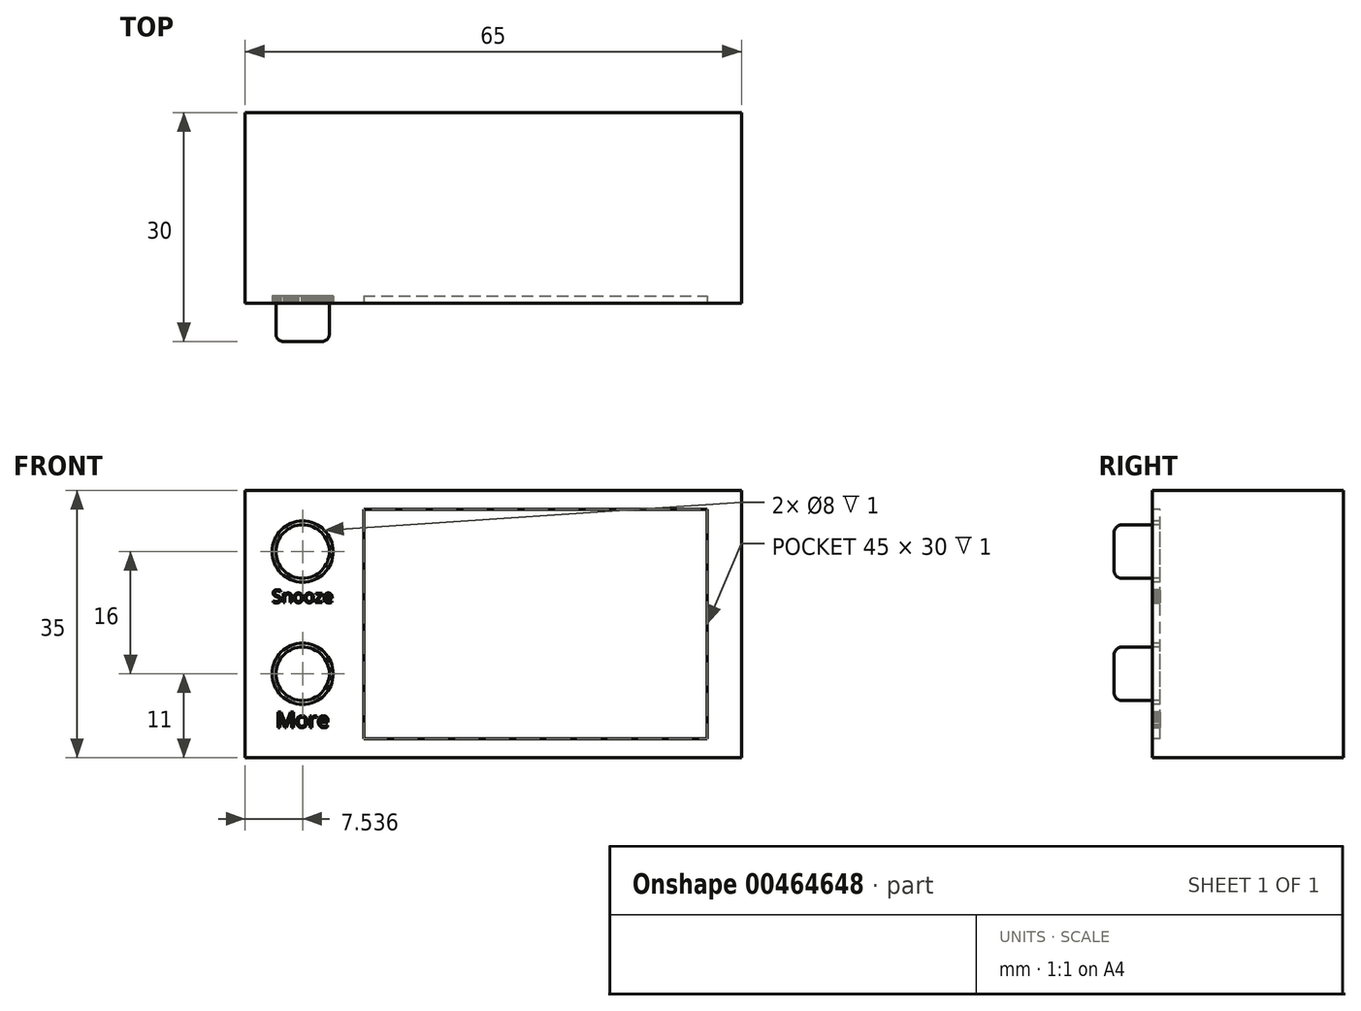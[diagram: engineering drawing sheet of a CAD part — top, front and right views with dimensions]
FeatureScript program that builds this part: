
annotation { "Feature Type Name" : "Feature", "Feature Type Description" : "" }
export const myFeature = defineFeature(function(context is Context, id is Id, definition is map)
    precondition{}
    {
        {
            var Q0;
            Q0=qCreatedBy(makeId("Front.planeOp"),FACE);
            var sketch = newSketch(context, id + "F0", { "sketchPlane" : qUnion([Q0])});
            skLineSegment(sketch, "E0.bottom", {"start": v(-32.5, 17.5) * mm, "end": v(32.5, 17.5) * mm});
            skLineSegment(sketch, "E0.top", {"start": v(-32.5, -17.5) * mm, "end": v(32.5, -17.5) * mm});
            skLineSegment(sketch, "E0.left", {"start": v(-32.5, 17.5) * mm, "end": v(-32.5, -17.5) * mm});
            skLineSegment(sketch, "E0.right", {"start": v(32.5, 17.5) * mm, "end": v(32.5, -17.5) * mm});
            skPoint(sketch, "E0.middle", {"position": v(0, 0) * mm});
            skPoint(sketch, "E1", {"position": v(0, 17.5) * mm});
            skPoint(sketch, "E2.middle", {"position": v(5.71, 0) * mm});
            skSolve(sketch);
        }
        {
            var Q0;
            Q0=makeQuery(id+"F0.imprint","IMPRINT",FACE,{"disambiguationData":[TD([[makeQuery(id+"F0.imprint","IMPRINT",EDGE,{"derivedFrom":sQuery(id+"F0.wireOp",EDGE,"E0.bottom")}),-1.0]])]});
            extrude(context, id + "F1", {"entities" : qUnion([Q0]), "oppositeDirection" : true, "depth" : 25 * mm});
        }
        {
            var Q0;
            Q0=qCreatedBy(makeId("Front.planeOp"),FACE);
            var sketch = newSketch(context, id + "F2", { "sketchPlane" : qUnion([Q0])});
            skLineSegment(sketch, "E3.bottom", {"start": v(-32.5, 17.5) * mm, "end": v(32.5, 17.5) * mm});
            skLineSegment(sketch, "E3.top", {"start": v(-32.5, -17.5) * mm, "end": v(32.5, -17.5) * mm});
            skLineSegment(sketch, "E3.left", {"start": v(-32.5, 17.5) * mm, "end": v(-32.5, -17.5) * mm});
            skLineSegment(sketch, "E3.right", {"start": v(32.5, 17.5) * mm, "end": v(32.5, -17.5) * mm});
            skPoint(sketch, "E3.middle", {"position": v(0, 0) * mm});
            skPoint(sketch, "E4", {"position": v(0, 17.5) * mm});
            skLineSegment(sketch, "E5.bottom", {"start": v(-16.96, -15) * mm, "end": v(28.04, -15) * mm});
            skLineSegment(sketch, "E5.top", {"start": v(-16.96, 15) * mm, "end": v(28.04, 15) * mm});
            skLineSegment(sketch, "E5.left", {"start": v(-16.96, -15) * mm, "end": v(-16.96, 15) * mm});
            skLineSegment(sketch, "E5.right", {"start": v(28.04, -15) * mm, "end": v(28.04, 15) * mm});
            skPoint(sketch, "E5.middle", {"position": v(5.54, 0) * mm});
            skCircle(sketch, "E6", {"center": v(-24.96, 9.5) * mm, "radius": 4 * mm});
            skCircle(sketch, "E7", {"center": v(-24.96, -6.5) * mm, "radius": 4 * mm});
            skText(sketch, "E8", { "text": "Snooze\n", "fontName": "OpenSans-Regular.ttf"});
            skText(sketch, "E9", { "text": "More\n", "fontName": "OpenSans-Regular.ttf"});
            skCircle(sketch, "E10", {"center": v(-24.96, 9.5) * mm, "radius": 3.5 * mm});
            skCircle(sketch, "E11", {"center": v(-24.96, -6.5) * mm, "radius": 3.5 * mm});
            const initialGuessF2  = {"E8": [-0.02896, 0.00281, 1, 0, 0.00169], "E9": [-0.02846, -0.01353, 1, 0, 0.00203]};
            skSetInitialGuess(sketch, initialGuessF2);
            skSolve(sketch);
        }
        {
            var Q0;
            Q0=makeQuery(id+"F2.imprint","IMPRINT",FACE,{"disambiguationData":[TD([[makeQuery(id+"F2.imprint","IMPRINT",EDGE,{"derivedFrom":sQuery(id+"F2.wireOp",EDGE,"E5.bottom")}),1.0]])]});
            extrude(context, id + "F3", {"entities" : qUnion([Q0]), "operationType" : NewBodyOperationType.REMOVE, "oppositeDirection" : true, "depth" : 1 * mm});
        }
        {
            var Q0;
            Q0=makeQuery(id+"F2.imprint","IMPRINT",FACE,{"disambiguationData":[TD([[makeQuery(id+"F2.imprint","IMPRINT",EDGE,{"derivedFrom":sQuery(id+"F2.wireOp",EDGE,"E6")}),1.0]])]});
            var Q1;
            Q1=makeQuery(id+"F2.imprint","IMPRINT",FACE,{"disambiguationData":[TD([[makeQuery(id+"F2.imprint","IMPRINT",EDGE,{"derivedFrom":sQuery(id+"F2.wireOp",EDGE,"E7")}),1.0]])]});
            extrude(context, id + "F4", {"entities" : qUnion([Q0, Q1]), "operationType" : NewBodyOperationType.REMOVE, "oppositeDirection" : true, "depth" : 1 * mm});
        }
        {
            var Q0;
            Q0=makeQuery(id+"F2.imprint","IMPRINT",FACE,{"disambiguationData":[TD([[makeQuery(id+"F2.imprint","IMPRINT",EDGE,{"derivedFrom":sQuery(id+"F2.wireOp",EDGE,"E10")}),1.0]])]});
            var Q1;
            Q1=makeQuery(id+"F2.imprint","IMPRINT",FACE,{"disambiguationData":[TD([[makeQuery(id+"F2.imprint","IMPRINT",EDGE,{"derivedFrom":sQuery(id+"F2.wireOp",EDGE,"E11")}),1.0]])]});
            extrude(context, id + "F5", {"entities" : qUnion([Q0, Q1]), "depth" : 5 * mm});
        }
        {
            var Q0;
            Q0=makeQuery(id+"F2.imprint","IMPRINT",FACE,{"disambiguationData":[TD([[makeQuery(id+"F2.imprint","IMPRINT",EDGE,{"derivedFrom":sQuery(id+"F2.wireOp",EDGE,"E8.sketch_text.stroke-0")}),-1.0]])]});
            var Q1;
            Q1=makeQuery(id+"F2.imprint","IMPRINT",FACE,{"disambiguationData":[TD([[makeQuery(id+"F2.imprint","IMPRINT",EDGE,{"derivedFrom":sQuery(id+"F2.wireOp",EDGE,"E8.sketch_text.stroke-18")}),-1.0]])]});
            var Q2;
            Q2=makeQuery(id+"F2.imprint","IMPRINT",FACE,{"disambiguationData":[TD([[makeQuery(id+"F2.imprint","IMPRINT",EDGE,{"derivedFrom":sQuery(id+"F2.wireOp",EDGE,"E8.sketch_text.stroke-35")}),-1.0]])]});
            var Q3;
            Q3=makeQuery(id+"F2.imprint","IMPRINT",FACE,{"disambiguationData":[TD([[makeQuery(id+"F2.imprint","IMPRINT",EDGE,{"derivedFrom":sQuery(id+"F2.wireOp",EDGE,"E8.sketch_text.stroke-48")}),-1.0]])]});
            var Q4;
            Q4=makeQuery(id+"F2.imprint","IMPRINT",FACE,{"disambiguationData":[TD([[makeQuery(id+"F2.imprint","IMPRINT",EDGE,{"derivedFrom":sQuery(id+"F2.wireOp",EDGE,"E9.sketch_text.stroke-0")}),-1.0]])]});
            var Q5;
            Q5=makeQuery(id+"F2.imprint","IMPRINT",FACE,{"disambiguationData":[TD([[makeQuery(id+"F2.imprint","IMPRINT",EDGE,{"derivedFrom":sQuery(id+"F2.wireOp",EDGE,"E9.sketch_text.stroke-10")}),-1.0]])]});
            var Q6;
            Q6=makeQuery(id+"F2.imprint","IMPRINT",FACE,{"disambiguationData":[TD([[makeQuery(id+"F2.imprint","IMPRINT",EDGE,{"derivedFrom":sQuery(id+"F2.wireOp",EDGE,"E9.sketch_text.stroke-20")}),-1.0]])]});
            var Q7;
            Q7=makeQuery(id+"F2.imprint","IMPRINT",FACE,{"disambiguationData":[TD([[makeQuery(id+"F2.imprint","IMPRINT",EDGE,{"derivedFrom":sQuery(id+"F2.wireOp",EDGE,"E8.sketch_text.stroke-59")}),-1.0]])]});
            var Q8;
            Q8=makeQuery(id+"F2.imprint","IMPRINT",FACE,{"disambiguationData":[TD([[makeQuery(id+"F2.imprint","IMPRINT",EDGE,{"derivedFrom":sQuery(id+"F2.wireOp",EDGE,"E8.sketch_text.stroke-76")}),-1.0]])]});
            var Q9;
            Q9=makeQuery(id+"F2.imprint","IMPRINT",FACE,{"disambiguationData":[TD([[makeQuery(id+"F2.imprint","IMPRINT",EDGE,{"derivedFrom":sQuery(id+"F2.wireOp",EDGE,"E8.sketch_text.stroke-86")}),-1.0]])]});
            var Q10;
            Q10=makeQuery(id+"F2.imprint","IMPRINT",FACE,{"disambiguationData":[TD([[makeQuery(id+"F2.imprint","IMPRINT",EDGE,{"derivedFrom":sQuery(id+"F2.wireOp",EDGE,"E9.sketch_text.stroke-35")}),-1.0]])]});
            var Q11;
            Q11=makeQuery(id+"F2.imprint","IMPRINT",FACE,{"disambiguationData":[TD([[makeQuery(id+"F2.imprint","IMPRINT",EDGE,{"derivedFrom":sQuery(id+"F2.wireOp",EDGE,"E9.sketch_text.stroke-48")}),-1.0]])]});
            extrude(context, id + "F6", {"entities" : qUnion([Q0, Q1, Q2, Q3, Q4, Q5, Q6, Q7, Q8, Q9, Q10, Q11]), "operationType" : NewBodyOperationType.REMOVE, "oppositeDirection" : true, "depth" : 1 * mm});
        }
        {
            var Q0;
            Q0=makeQuery(id+"F5.opExtrude","CAP_EDGE",EDGE,{"disambiguationData":[OSD([sQuery(id+"F2.wireOp",EDGE,"E10")])],"isStart":false});
            var Q1;
            Q1=makeQuery(id+"F5.opExtrude","CAP_EDGE",EDGE,{"disambiguationData":[OSD([sQuery(id+"F2.wireOp",EDGE,"E11")])],"isStart":false});
            fillet(context, id + "F7", {"entities" : qUnion([Q0, Q1]), "radius" : 1 * mm, "tangentPropagation" : true, "allowEdgeOverflow" : false});
        }
        {
            var Q0;
            Q0=makeQuery(id+"F2.imprint","IMPRINT",FACE,{"disambiguationData":[TD([[makeQuery(id+"F2.imprint","IMPRINT",EDGE,{"derivedFrom":sQuery(id+"F2.wireOp",EDGE,"E5.bottom")}),1.0]])]});
            extrude(context, id + "F8", {"entities" : qUnion([Q0]), "oppositeDirection" : true, "depth" : .5 * mm});
        }
        {
            var Q0;
            Q0=makeQuery(id+"F8.opExtrude","SWEPT_BODY",BODY,{"disambiguationData":[OSD([sQuery(id+"F2.wireOp",EDGE,"E5.bottom"),sQuery(id+"F2.wireOp",EDGE,"E5.top"),sQuery(id+"F2.wireOp",EDGE,"E5.left"),sQuery(id+"F2.wireOp",EDGE,"E5.right")])]});
            transform(context, id + "F9", {"entities" : qUnion([Q0]), "transformType" : TransformType.TRANSLATION_3D, "dx" : 0 * mm, "dy" : .5 * mm, "dz" : 0 * mm, "makeCopy" : false});
        }
        {
            var Q0;
            Q0=makeQuery(id+"F8.opExtrude","SWEPT_BODY",BODY,{"disambiguationData":[OSD([sQuery(id+"F2.wireOp",EDGE,"E5.bottom"),sQuery(id+"F2.wireOp",EDGE,"E5.top"),sQuery(id+"F2.wireOp",EDGE,"E5.left"),sQuery(id+"F2.wireOp",EDGE,"E5.right")])]});
            deleteBodies(context, id + "F10", {"entities" : qUnion([Q0])});
        }
    });
